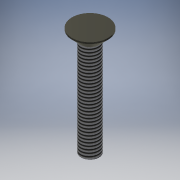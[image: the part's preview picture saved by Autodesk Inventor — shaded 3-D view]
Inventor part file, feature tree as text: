
AUTODESK INVENTOR PART (.ipt)
format: ipt  version: 2020.2 (Build 242310000, 310)  size: 135,168 bytes
history: native  units: mm
features: extrude x5, sketch x5, other x1, thread x1, chamfer x1
ambient origin geometry x1: Origin
bodies: Body1 (feature_tree)
feature tree (13):
  other  "ソリッド1"
  extrude  "押し出し1"  Depth=3.0mm
  extrude  "押し出し2"  Depth=6.0mm TaperAngle=0.0deg
  thread  "ねじ1"
  chamfer  "面取り1"  Distance=6.0mm
  extrude  "押し出し4"  Depth=1.75mm TaperAngle=0.0deg
  extrude  "押し出し5"  Depth=10.0mm TaperAngle=0.0deg
  extrude  "押し出し6"  Depth=1.5mm TaperAngle=45.0deg
  sketch  "スケッチ1"
  sketch  "スケッチ2"
  sketch  "スケッチ4"
  sketch  "スケッチ5"
  sketch  "スケッチ6"
